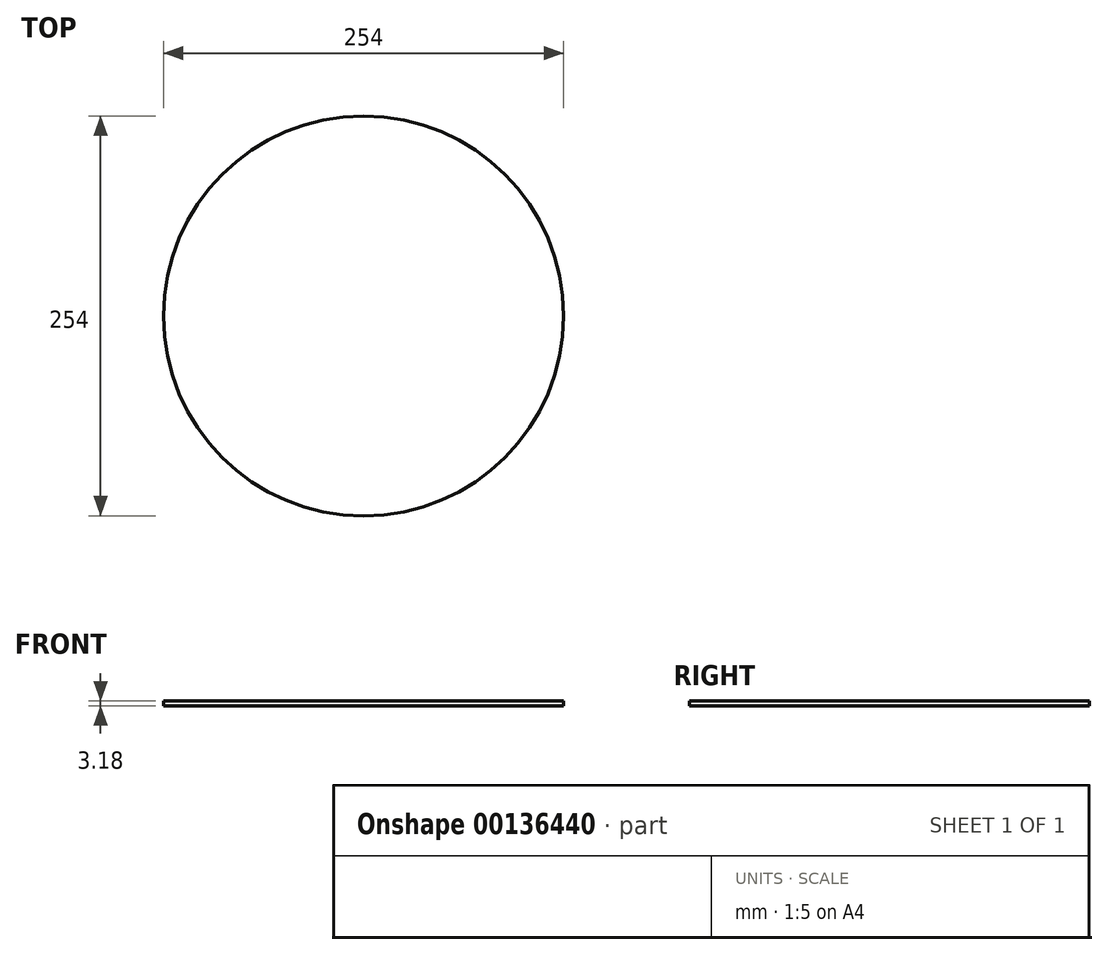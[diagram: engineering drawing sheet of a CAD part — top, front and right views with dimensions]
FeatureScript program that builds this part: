
annotation { "Feature Type Name" : "Feature", "Feature Type Description" : "" }
export const myFeature = defineFeature(function(context is Context, id is Id, definition is map)
    precondition{}
    {
        {
            var Q0;
            Q0=qCreatedBy(makeId("Top.planeOp"),FACE);
            var sketch = newSketch(context, id + "F0", { "sketchPlane" : qUnion([Q0])});
            skCircle(sketch, "E0", {"center": v(0, 0) * mm, "radius": 127 * mm});
            skSolve(sketch);
        }
        {
            var Q0;
            Q0=makeQuery(id+"F0.imprint","IMPRINT",FACE,{"disambiguationData":[TD([[makeQuery(id+"F0.imprint","IMPRINT",EDGE,{"derivedFrom":sQuery(id+"F0.wireOp",EDGE,"E0")}),1.0]])]});
            extrude(context, id + "F1", {"entities" : qUnion([Q0]), "depth" : 3.17 * mm});
        }
    });
